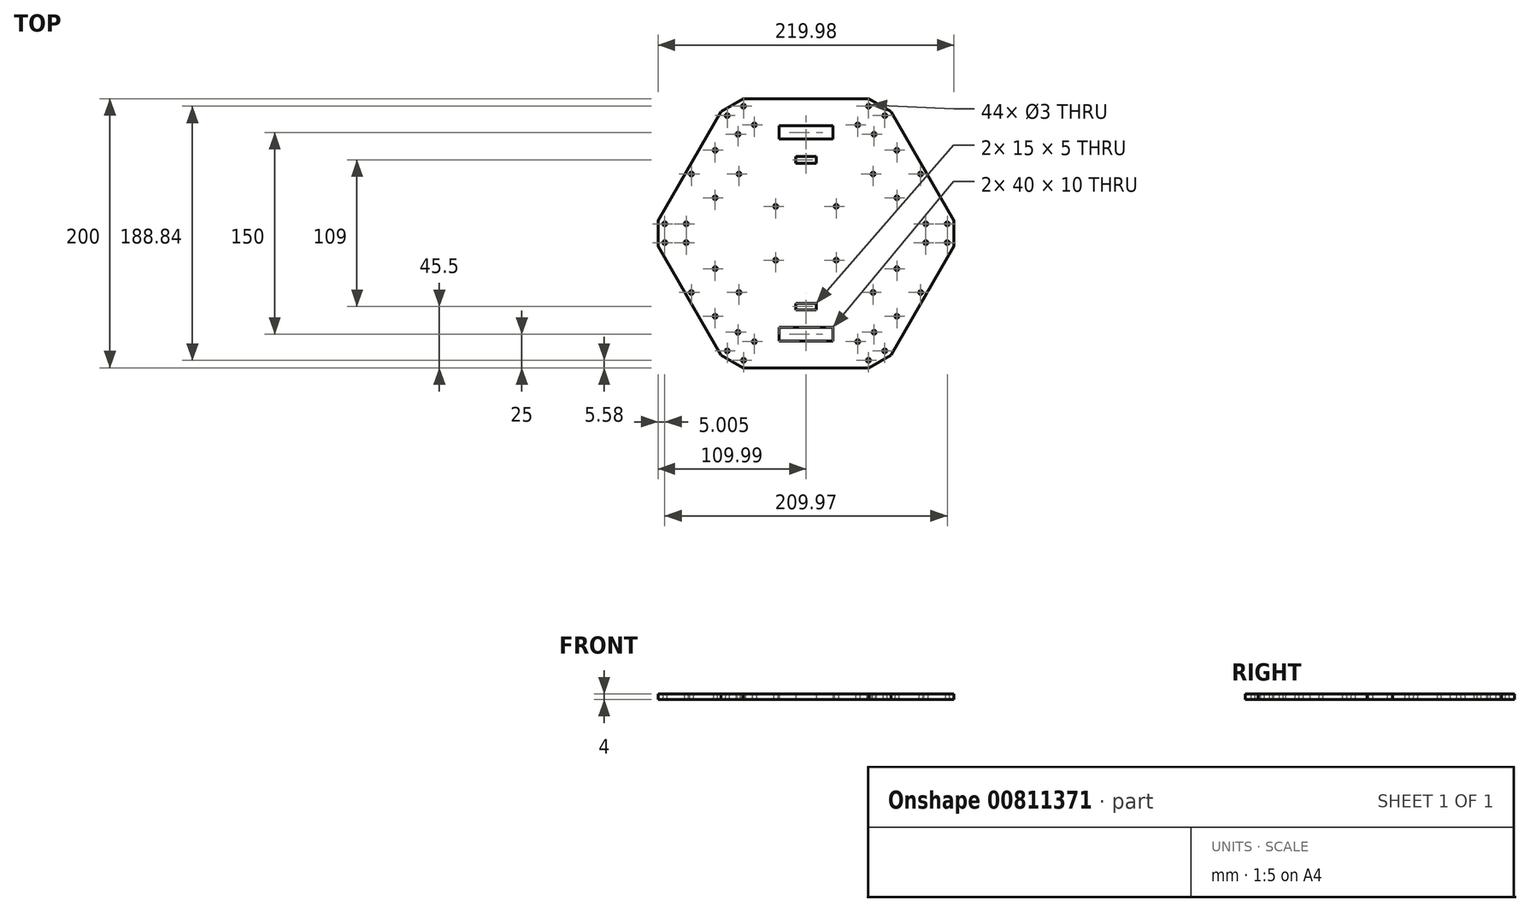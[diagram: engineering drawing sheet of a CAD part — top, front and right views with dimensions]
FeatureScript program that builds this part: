
annotation { "Feature Type Name" : "Feature", "Feature Type Description" : "" }
export const myFeature = defineFeature(function(context is Context, id is Id, definition is map)
    precondition{}
    {
        {
            var Q0;
            Q0=qCreatedBy(makeId("Top.planeOp"),FACE);
            var sketch = newSketch(context, id + "F0", { "sketchPlane" : qUnion([Q0])});
            skCircle(sketch, "E0.cCircle", {"center": v(0, 0) * mm, "radius": 100 * mm, "construction": true});
            skLineSegment(sketch, "E0.0", {"start": v(57.74, -100) * mm, "end": v(-57.74, -100) * mm});
            skLineSegment(sketch, "E0.1", {"start": v(-57.74, -100) * mm, "end": v(-115.47, 0) * mm});
            skLineSegment(sketch, "E0.2", {"start": v(-115.47, 0) * mm, "end": v(-57.74, 100) * mm});
            skLineSegment(sketch, "E0.3", {"start": v(-57.74, 100) * mm, "end": v(57.74, 100) * mm});
            skLineSegment(sketch, "E0.4", {"start": v(57.74, 100) * mm, "end": v(115.47, 0) * mm});
            skLineSegment(sketch, "E0.5", {"start": v(115.47, 0) * mm, "end": v(57.74, -100) * mm});
            skPoint(sketch, "E0.0.midPoint", {"position": v(0, -100) * mm});
            skLineSegment(sketch, "E1", {"start": v(-63.22, 90.5) * mm, "end": v(-46.77, 100) * mm});
            skLineSegment(sketch, "E2.1.0", {"start": v(-109.99, -9.5) * mm, "end": v(-109.99, 9.5) * mm});
            skLineSegment(sketch, "E2.2.0", {"start": v(-46.77, -100) * mm, "end": v(-63.22, -90.5) * mm});
            skLineSegment(sketch, "E2.3.0", {"start": v(63.22, -90.5) * mm, "end": v(46.77, -100) * mm});
            skLineSegment(sketch, "E2.4.0", {"start": v(109.99, 9.5) * mm, "end": v(109.99, -9.5) * mm});
            skLineSegment(sketch, "E2.5.0", {"start": v(46.77, 100) * mm, "end": v(63.22, 90.5) * mm});
            skLineSegment(sketch, "E3", {"start": v(-55, 95.25) * mm, "end": v(-57.74, 100) * mm});
            skLineSegment(sketch, "E4.bottom", {"start": v(22.5, 20) * mm, "end": v(-22.5, 20) * mm});
            skLineSegment(sketch, "E4.top", {"start": v(22.5, -20) * mm, "end": v(-22.5, -20) * mm});
            skLineSegment(sketch, "E4.left", {"start": v(22.5, 20) * mm, "end": v(22.5, -20) * mm});
            skLineSegment(sketch, "E4.right", {"start": v(-22.5, 20) * mm, "end": v(-22.5, -20) * mm});
            skCircle(sketch, "E5", {"center": v(-22.5, 20) * mm, "radius": 1.5 * mm});
            skCircle(sketch, "E6", {"center": v(22.5, 20) * mm, "radius": 1.5 * mm});
            skCircle(sketch, "E7", {"center": v(22.5, -20) * mm, "radius": 1.5 * mm});
            skCircle(sketch, "E8", {"center": v(-22.5, -20) * mm, "radius": 1.5 * mm});
            skLineSegment(sketch, "E9.bottom", {"start": v(18, -52) * mm, "end": v(-18, -52) * mm});
            skLineSegment(sketch, "E9.top", {"start": v(18, 52) * mm, "end": v(-18, 52) * mm});
            skLineSegment(sketch, "E9.left", {"start": v(18, -52) * mm, "end": v(18, 52) * mm});
            skLineSegment(sketch, "E9.right", {"start": v(-18, -52) * mm, "end": v(-18, 52) * mm});
            skLineSegment(sketch, "E10.bottom", {"start": v(7.5, 47) * mm, "end": v(-7.5, 47) * mm});
            skLineSegment(sketch, "E10.top", {"start": v(7.5, 57) * mm, "end": v(-7.5, 57) * mm});
            skLineSegment(sketch, "E10.left", {"start": v(7.5, 47) * mm, "end": v(7.5, 57) * mm});
            skLineSegment(sketch, "E10.right", {"start": v(-7.5, 47) * mm, "end": v(-7.5, 57) * mm});
            skPoint(sketch, "E10.middle", {"position": v(0, 52) * mm});
            skLineSegment(sketch, "E11.bottom", {"start": v(7.5, -57) * mm, "end": v(-7.5, -57) * mm});
            skLineSegment(sketch, "E11.top", {"start": v(7.5, -47) * mm, "end": v(-7.5, -47) * mm});
            skLineSegment(sketch, "E11.left", {"start": v(7.5, -57) * mm, "end": v(7.5, -47) * mm});
            skLineSegment(sketch, "E11.right", {"start": v(-7.5, -57) * mm, "end": v(-7.5, -47) * mm});
            skPoint(sketch, "E11.middle", {"position": v(0, -52) * mm});
            skLineSegment(sketch, "E12.bottom", {"start": v(20, 70) * mm, "end": v(-20, 70) * mm});
            skLineSegment(sketch, "E12.top", {"start": v(20, 80) * mm, "end": v(-20, 80) * mm});
            skLineSegment(sketch, "E12.left", {"start": v(20, 70) * mm, "end": v(20, 80) * mm});
            skLineSegment(sketch, "E12.right", {"start": v(-20, 70) * mm, "end": v(-20, 80) * mm});
            skPoint(sketch, "E12.middle", {"position": v(0, 75) * mm});
            skPoint(sketch, "E12.middle.positionSnap0", {"position": v(0, 57) * mm});
            skPoint(sketch, "E12.centerSnap0", {"position": v(0, 57) * mm});
            skLineSegment(sketch, "E13.MirrorCS", {"start": v(-20, -70) * mm, "end": v(-20, -80) * mm});
            skLineSegment(sketch, "E14.MirrorCS", {"start": v(20, -80) * mm, "end": v(-20, -80) * mm});
            skLineSegment(sketch, "E15.MirrorCS", {"start": v(20, -70) * mm, "end": v(-20, -70) * mm});
            skLineSegment(sketch, "E16.MirrorCS", {"start": v(20, -70) * mm, "end": v(20, -80) * mm});
            skLineSegment(sketch, "E17.bottom", {"start": v(-67.5, 44) * mm, "end": v(67.5, 44) * mm});
            skLineSegment(sketch, "E17.top", {"start": v(-67.5, -44) * mm, "end": v(67.5, -44) * mm});
            skLineSegment(sketch, "E17.left", {"start": v(-67.5, 44) * mm, "end": v(-67.5, -44) * mm});
            skLineSegment(sketch, "E17.right", {"start": v(67.5, 44) * mm, "end": v(67.5, -44) * mm});
            skLineSegment(sketch, "E18", {"start": v(-67.5, 26.32) * mm, "end": v(-49.82, 44) * mm});
            skLineSegment(sketch, "E19", {"start": v(-49.82, 44) * mm, "end": v(-67.5, 61.68) * mm});
            skLineSegment(sketch, "E20", {"start": v(-67.5, 61.68) * mm, "end": v(-85.18, 44) * mm});
            skLineSegment(sketch, "E21", {"start": v(-85.18, 44) * mm, "end": v(-67.5, 26.32) * mm});
            skCircle(sketch, "E22", {"center": v(-67.5, 61.68) * mm, "radius": 1.5 * mm});
            skCircle(sketch, "E23", {"center": v(-49.82, 44) * mm, "radius": 1.5 * mm});
            skCircle(sketch, "E24", {"center": v(-67.5, 26.32) * mm, "radius": 1.5 * mm});
            skCircle(sketch, "E25", {"center": v(-85.18, 44) * mm, "radius": 1.5 * mm});
            skCircle(sketch, "E26.MirrorC", {"center": v(49.82, 44) * mm, "radius": 1.5 * mm});
            skCircle(sketch, "E27.MirrorC", {"center": v(67.5, 61.68) * mm, "radius": 1.5 * mm});
            skCircle(sketch, "E28.MirrorC", {"center": v(85.18, 44) * mm, "radius": 1.5 * mm});
            skCircle(sketch, "E29.MirrorC", {"center": v(67.5, 26.32) * mm, "radius": 1.5 * mm});
            skCircle(sketch, "E30.MirrorC", {"center": v(-67.5, -26.32) * mm, "radius": 1.5 * mm});
            skCircle(sketch, "E31.MirrorC", {"center": v(-85.18, -44) * mm, "radius": 1.5 * mm});
            skCircle(sketch, "E32.MirrorC", {"center": v(-67.5, -61.68) * mm, "radius": 1.5 * mm});
            skCircle(sketch, "E33.MirrorC", {"center": v(-49.82, -44) * mm, "radius": 1.5 * mm});
            skCircle(sketch, "E34.MirrorC", {"center": v(49.82, -44) * mm, "radius": 1.5 * mm});
            skCircle(sketch, "E35.MirrorC", {"center": v(67.5, -26.32) * mm, "radius": 1.5 * mm});
            skCircle(sketch, "E36.MirrorC", {"center": v(85.18, -44) * mm, "radius": 1.5 * mm});
            skCircle(sketch, "E37.MirrorC", {"center": v(67.5, -61.68) * mm, "radius": 1.5 * mm});
            skLineSegment(sketch, "E38.bottom", {"start": v(-88.99, -7) * mm, "end": v(-104.99, -7) * mm});
            skLineSegment(sketch, "E38.top", {"start": v(-88.99, 7) * mm, "end": v(-104.99, 7) * mm});
            skLineSegment(sketch, "E38.left", {"start": v(-88.99, -7) * mm, "end": v(-88.99, 7) * mm});
            skLineSegment(sketch, "E38.right", {"start": v(-104.99, -7) * mm, "end": v(-104.99, 7) * mm});
            skPoint(sketch, "E38.middle", {"position": v(-96.99, 0) * mm});
            skPoint(sketch, "E38.middle.positionSnap0", {"position": v(-109.99, 0) * mm});
            skPoint(sketch, "E38.centerSnap0", {"position": v(-109.99, 0) * mm});
            skCircle(sketch, "E39", {"center": v(-104.99, 7) * mm, "radius": 1.5 * mm});
            skCircle(sketch, "E40", {"center": v(-88.99, 7) * mm, "radius": 1.5 * mm});
            skCircle(sketch, "E41", {"center": v(-104.99, -7) * mm, "radius": 1.5 * mm});
            skCircle(sketch, "E42", {"center": v(-88.99, -7) * mm, "radius": 1.5 * mm});
            skCircle(sketch, "E43.1.0", {"center": v(-58.55, -87.42) * mm, "radius": 1.5 * mm});
            skCircle(sketch, "E43.1.1", {"center": v(-50.55, -73.56) * mm, "radius": 1.5 * mm});
            skCircle(sketch, "E43.1.2", {"center": v(-38.43, -80.56) * mm, "radius": 1.5 * mm});
            skCircle(sketch, "E43.1.3", {"center": v(-46.43, -94.42) * mm, "radius": 1.5 * mm});
            skCircle(sketch, "E43.2.0", {"center": v(46.43, -94.42) * mm, "radius": 1.5 * mm});
            skCircle(sketch, "E43.2.1", {"center": v(38.43, -80.56) * mm, "radius": 1.5 * mm});
            skCircle(sketch, "E43.2.2", {"center": v(50.55, -73.56) * mm, "radius": 1.5 * mm});
            skCircle(sketch, "E43.2.3", {"center": v(58.55, -87.42) * mm, "radius": 1.5 * mm});
            skCircle(sketch, "E43.3.0", {"center": v(104.99, -7) * mm, "radius": 1.5 * mm});
            skCircle(sketch, "E43.3.1", {"center": v(88.99, -7) * mm, "radius": 1.5 * mm});
            skCircle(sketch, "E43.3.2", {"center": v(88.99, 7) * mm, "radius": 1.5 * mm});
            skCircle(sketch, "E43.3.3", {"center": v(104.99, 7) * mm, "radius": 1.5 * mm});
            skCircle(sketch, "E43.4.0", {"center": v(58.55, 87.42) * mm, "radius": 1.5 * mm});
            skCircle(sketch, "E43.4.1", {"center": v(50.55, 73.56) * mm, "radius": 1.5 * mm});
            skCircle(sketch, "E43.4.2", {"center": v(38.43, 80.56) * mm, "radius": 1.5 * mm});
            skCircle(sketch, "E43.4.3", {"center": v(46.43, 94.42) * mm, "radius": 1.5 * mm});
            skCircle(sketch, "E43.5.0", {"center": v(-46.43, 94.42) * mm, "radius": 1.5 * mm});
            skCircle(sketch, "E43.5.1", {"center": v(-38.43, 80.56) * mm, "radius": 1.5 * mm});
            skCircle(sketch, "E43.5.2", {"center": v(-50.55, 73.56) * mm, "radius": 1.5 * mm});
            skCircle(sketch, "E43.5.3", {"center": v(-58.55, 87.42) * mm, "radius": 1.5 * mm});
            skSolve(sketch);
        }
        {
            var Q0;
            {var subQ9=sQuery(id+"F0.wireOp",EDGE,"E2.1.0");Q0=makeQuery(id+"F0.imprint","IMPRINT",FACE,{"disambiguationData":[TD([[makeQuery(id+"F0.imprint","IMPRINT",EDGE,{"derivedFrom":subQ9}),-1.0]])]});}
            var Q1;
            {var subQ9=sQuery(id+"F0.wireOp",EDGE,"bfc2ec8a-7ca7-4c05-844f-46ad19fef504.top");var subQ10=sQuery(id+"F0.wireOp",EDGE,"6be4e249-8f7a-452a-a771-35af0030ee52.1.0");var subQ11=makeQuery(id+"F0.imprint","INTERSECT",VERTEX,{"derivedFrom":[subQ10,subQ9]});Q1=makeQuery(id+"F0.imprint","IMPRINT",FACE,{"disambiguationData":[TD([[makeQuery(id+"F0.imprint","IMPRINT",EDGE,{"disambiguationData":[TD([[subQ11,-1.0]])],"derivedFrom":subQ10}),-1.0]])]});}
            var Q2;
            {var subQ5=sQuery(id+"F0.wireOp",EDGE,"E6");var subQ13=sQuery(id+"F0.wireOp",EDGE,"E4.bottom");var subQ14=makeQuery(id+"F0.imprint","INTERSECT",VERTEX,{"derivedFrom":[subQ13,subQ5]});Q2=makeQuery(id+"F0.imprint","IMPRINT",FACE,{"disambiguationData":[TD([[makeQuery(id+"F0.imprint","IMPRINT",EDGE,{"disambiguationData":[TD([[subQ14,-1.0]])],"derivedFrom":subQ13}),1.0]])]});}
            var Q3;
            {var subQ5=sQuery(id+"F0.wireOp",EDGE,"E10.bottom");Q3=makeQuery(id+"F0.imprint","IMPRINT",FACE,{"disambiguationData":[TD([[makeQuery(id+"F0.imprint","IMPRINT",EDGE,{"derivedFrom":subQ5}),1.0]])]});}
            var Q4;
            {var subQ5=sQuery(id+"F0.wireOp",EDGE,"E10.bottom");Q4=makeQuery(id+"F0.imprint","IMPRINT",FACE,{"disambiguationData":[TD([[makeQuery(id+"F0.imprint","IMPRINT",EDGE,{"derivedFrom":subQ5}),-1.0]])]});}
            var Q5;
            {var subQ1=sQuery(id+"F0.wireOp",EDGE,"E4.bottom");var subQ7=sQuery(id+"F0.wireOp",EDGE,"E9.right");var subQ8=makeQuery(id+"F0.imprint","INTERSECT",VERTEX,{"derivedFrom":[subQ1,subQ7]});Q5=makeQuery(id+"F0.imprint","IMPRINT",FACE,{"disambiguationData":[TD([[makeQuery(id+"F0.imprint","IMPRINT",EDGE,{"disambiguationData":[TD([[subQ8,-1.0]])],"derivedFrom":subQ1}),1.0]])]});}
            var Q6;
            {var subQ12=sQuery(id+"F0.wireOp",EDGE,"E11.top");Q6=makeQuery(id+"F0.imprint","IMPRINT",FACE,{"disambiguationData":[TD([[makeQuery(id+"F0.imprint","IMPRINT",EDGE,{"derivedFrom":subQ12}),-1.0]])]});}
            var Q7;
            {var subQ0=sQuery(id+"F0.wireOp",EDGE,"E9.left");var subQ1=sQuery(id+"F0.wireOp",EDGE,"E4.bottom");var subQ2=makeQuery(id+"F0.imprint","INTERSECT",VERTEX,{"derivedFrom":[subQ1,subQ0]});Q7=makeQuery(id+"F0.imprint","IMPRINT",FACE,{"disambiguationData":[TD([[makeQuery(id+"F0.imprint","IMPRINT",EDGE,{"disambiguationData":[TD([[subQ2,-1.0]])],"derivedFrom":subQ1}),1.0]])]});}
            var Q8;
            {var subQ5=sQuery(id+"F0.wireOp",EDGE,"E11.top");Q8=makeQuery(id+"F0.imprint","IMPRINT",FACE,{"disambiguationData":[TD([[makeQuery(id+"F0.imprint","IMPRINT",EDGE,{"derivedFrom":subQ5}),1.0]])]});}
            var Q9;
            {var subQ1=sQuery(id+"F0.wireOp",EDGE,"E9.right");var subQ18=sQuery(id+"F0.wireOp",EDGE,"E4.bottom");var subQ19=makeQuery(id+"F0.imprint","INTERSECT",VERTEX,{"derivedFrom":[subQ18,subQ1]});Q9=makeQuery(id+"F0.imprint","IMPRINT",FACE,{"disambiguationData":[TD([[makeQuery(id+"F0.imprint","IMPRINT",EDGE,{"disambiguationData":[TD([[subQ19,-1.0]])],"derivedFrom":subQ18}),-1.0]])]});}
            var Q10;
            {var subQ5=sQuery(id+"F0.wireOp",EDGE,"E17.left");var subQ6=sQuery(id+"F0.wireOp",EDGE,"E17.bottom");var subQ7=makeQuery(id+"F0.imprint","INTERSECT",VERTEX,{"derivedFrom":[subQ6,subQ5]});Q10=makeQuery(id+"F0.imprint","IMPRINT",FACE,{"disambiguationData":[TD([[makeQuery(id+"F0.imprint","IMPRINT",EDGE,{"disambiguationData":[TD([[subQ7,-1.0]])],"derivedFrom":subQ6}),1.0]])]});}
            var Q11;
            {var subQ1=sQuery(id+"F0.wireOp",EDGE,"E17.bottom");var subQ7=sQuery(id+"F0.wireOp",EDGE,"E17.left");var subQ8=makeQuery(id+"F0.imprint","INTERSECT",VERTEX,{"derivedFrom":[subQ1,subQ7]});Q11=makeQuery(id+"F0.imprint","IMPRINT",FACE,{"disambiguationData":[TD([[makeQuery(id+"F0.imprint","IMPRINT",EDGE,{"disambiguationData":[TD([[subQ8,-1.0]])],"derivedFrom":subQ1}),-1.0]])]});}
            var Q12;
            {var subQ12=sQuery(id+"F0.wireOp",EDGE,"E6");var subQ13=sQuery(id+"F0.wireOp",EDGE,"E4.bottom");var subQ14=makeQuery(id+"F0.imprint","INTERSECT",VERTEX,{"derivedFrom":[subQ13,subQ12]});Q12=makeQuery(id+"F0.imprint","IMPRINT",FACE,{"disambiguationData":[TD([[makeQuery(id+"F0.imprint","IMPRINT",EDGE,{"disambiguationData":[TD([[subQ14,-1.0]])],"derivedFrom":subQ13}),-1.0]])]});}
            var Q13;
            {var subQ0=sQuery(id+"F0.wireOp",EDGE,"E9.left");var subQ1=sQuery(id+"F0.wireOp",EDGE,"E4.bottom");var subQ2=makeQuery(id+"F0.imprint","INTERSECT",VERTEX,{"derivedFrom":[subQ1,subQ0]});Q13=makeQuery(id+"F0.imprint","IMPRINT",FACE,{"disambiguationData":[TD([[makeQuery(id+"F0.imprint","IMPRINT",EDGE,{"disambiguationData":[TD([[subQ2,-1.0]])],"derivedFrom":subQ1}),-1.0]])]});}
            var Q14;
            {var subQ0=sQuery(id+"F0.wireOp",EDGE,"E9.left");var subQ1=sQuery(id+"F0.wireOp",EDGE,"E4.top");var subQ2=makeQuery(id+"F0.imprint","INTERSECT",VERTEX,{"derivedFrom":[subQ1,subQ0]});Q14=makeQuery(id+"F0.imprint","IMPRINT",FACE,{"disambiguationData":[TD([[makeQuery(id+"F0.imprint","IMPRINT",EDGE,{"disambiguationData":[TD([[subQ2,-1.0]])],"derivedFrom":subQ1}),1.0]])]});}
            var Q15;
            {var subQ5=sQuery(id+"F0.wireOp",EDGE,"E42");var subQ10=sQuery(id+"F0.wireOp",EDGE,"E38.bottom");var subQ11=makeQuery(id+"F0.imprint","INTERSECT",VERTEX,{"derivedFrom":[subQ10,subQ5]});Q15=makeQuery(id+"F0.imprint","IMPRINT",FACE,{"disambiguationData":[TD([[makeQuery(id+"F0.imprint","IMPRINT",EDGE,{"disambiguationData":[TD([[subQ11,-1.0]])],"derivedFrom":subQ10}),-1.0]])]});}
            extrude(context, id + "F1", {"entities" : qUnion([Q0, Q1, Q2, Q3, Q4, Q5, Q6, Q7, Q8, Q9, Q10, Q11, Q12, Q13, Q14, Q15]), "depth" : 4 * mm, "offsetDistance" : 25 * mm});
        }
    });
